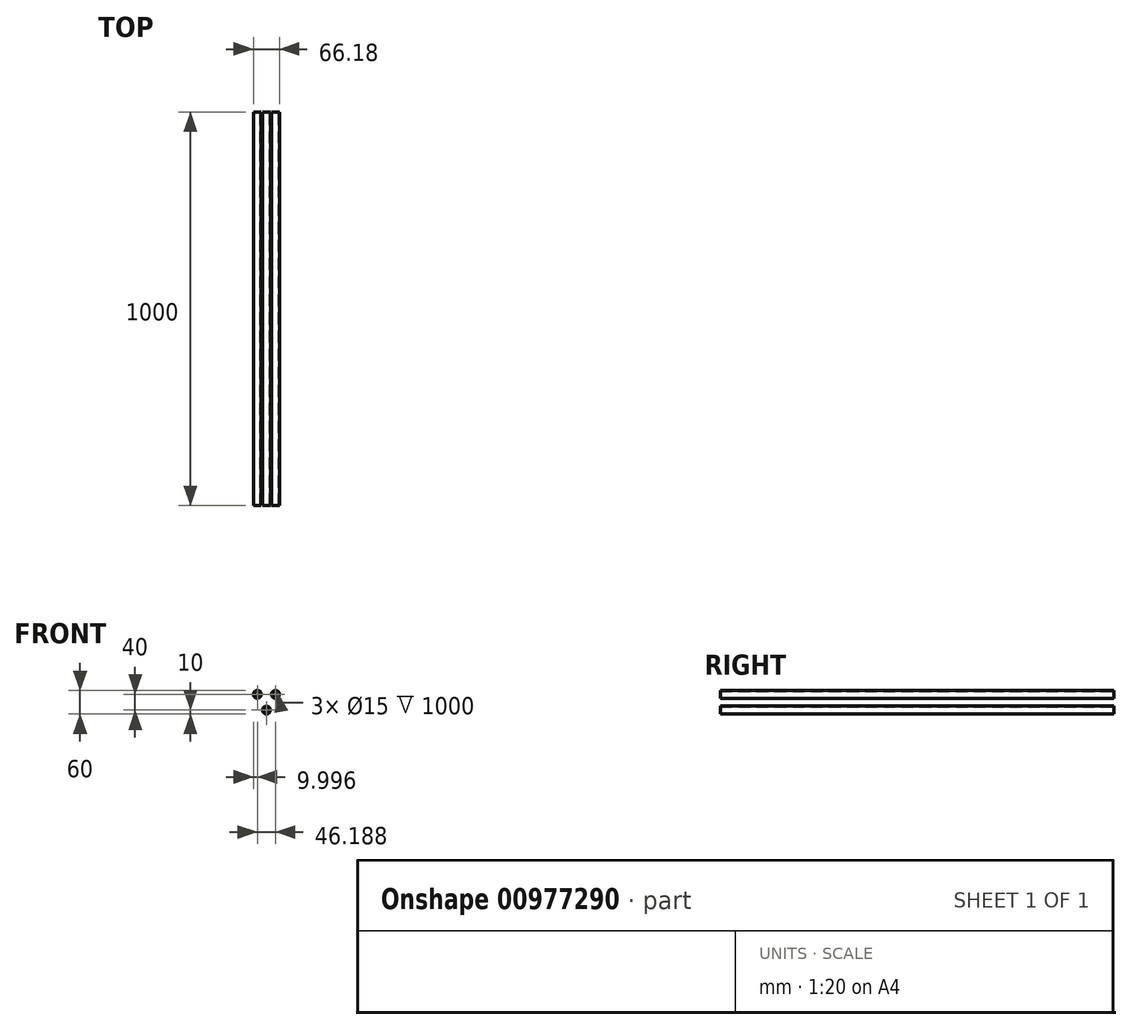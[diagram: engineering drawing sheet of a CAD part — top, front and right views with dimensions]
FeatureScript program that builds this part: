
annotation { "Feature Type Name" : "Feature", "Feature Type Description" : "" }
export const myFeature = defineFeature(function(context is Context, id is Id, definition is map)
    precondition{}
    {
        {
            var Q0;
            Q0=qCreatedBy(makeId("Front.planeOp"),FACE);
            var sketch = newSketch(context, id + "F0", { "sketchPlane" : qUnion([Q0])});
            skCircle(sketch, "E0", {"center": v(0, 0) * mm, "radius": 10 * mm});
            skCircle(sketch, "E1", {"center": v(23.1, 40) * mm, "radius": 10 * mm});
            skCircle(sketch, "E2", {"center": v(-23.1, 40) * mm, "radius": 10 * mm});
            skCircle(sketch, "E3", {"center": v(-23.1, 40) * mm, "radius": 15 * mm});
            skCircle(sketch, "E4", {"center": v(23.1, 40) * mm, "radius": 15 * mm});
            skCircle(sketch, "E5", {"center": v(0, 0) * mm, "radius": 15 * mm});
            skLineSegment(sketch, "E6", {"start": v(0, 0) * mm, "end": v(-23.1, 40) * mm});
            skLineSegment(sketch, "E7", {"start": v(23.1, 40) * mm, "end": v(0, 0) * mm});
            skLineSegment(sketch, "E8", {"start": v(-23.1, 40) * mm, "end": v(23.1, 40) * mm});
            skCircle(sketch, "E9", {"center": v(-23.1, 40) * mm, "radius": 7.5 * mm});
            skCircle(sketch, "E10", {"center": v(23.1, 40) * mm, "radius": 7.5 * mm});
            skCircle(sketch, "E11", {"center": v(0, 0) * mm, "radius": 7.5 * mm});
            skSolve(sketch);
        }
        {
            var Q0;
            {var subQ0=sQuery(id+"F0.wireOp",EDGE,"E6");var subQ1=sQuery(id+"F0.wireOp",EDGE,"E2");var subQ2=makeQuery(id+"F0.imprint","INTERSECT",VERTEX,{"derivedFrom":[subQ1,subQ0]});Q0=makeQuery(id+"F0.imprint","IMPRINT",FACE,{"disambiguationData":[TD([[makeQuery(id+"F0.imprint","IMPRINT",EDGE,{"disambiguationData":[TD([[subQ2,1.0]])],"derivedFrom":subQ1}),1.0]])]});}
            var Q1;
            {var subQ0=sQuery(id+"F0.wireOp",EDGE,"E6");var subQ1=sQuery(id+"F0.wireOp",EDGE,"E2");var subQ2=makeQuery(id+"F0.imprint","INTERSECT",VERTEX,{"derivedFrom":[subQ1,subQ0]});Q1=makeQuery(id+"F0.imprint","IMPRINT",FACE,{"disambiguationData":[TD([[makeQuery(id+"F0.imprint","IMPRINT",EDGE,{"disambiguationData":[TD([[subQ2,-1.0]])],"derivedFrom":subQ1}),1.0]])]});}
            var Q2;
            {var subQ0=sQuery(id+"F0.wireOp",EDGE,"E7");var subQ1=sQuery(id+"F0.wireOp",EDGE,"E1");var subQ2=makeQuery(id+"F0.imprint","INTERSECT",VERTEX,{"derivedFrom":[subQ1,subQ0]});Q2=makeQuery(id+"F0.imprint","IMPRINT",FACE,{"disambiguationData":[TD([[makeQuery(id+"F0.imprint","IMPRINT",EDGE,{"disambiguationData":[TD([[subQ2,-1.0]])],"derivedFrom":subQ1}),1.0]])]});}
            var Q3;
            {var subQ0=sQuery(id+"F0.wireOp",EDGE,"E7");var subQ1=sQuery(id+"F0.wireOp",EDGE,"E1");var subQ2=makeQuery(id+"F0.imprint","INTERSECT",VERTEX,{"derivedFrom":[subQ1,subQ0]});Q3=makeQuery(id+"F0.imprint","IMPRINT",FACE,{"disambiguationData":[TD([[makeQuery(id+"F0.imprint","IMPRINT",EDGE,{"disambiguationData":[TD([[subQ2,1.0]])],"derivedFrom":subQ1}),1.0]])]});}
            var Q4;
            {var subQ0=sQuery(id+"F0.wireOp",EDGE,"E6");var subQ1=sQuery(id+"F0.wireOp",EDGE,"E0");var subQ2=makeQuery(id+"F0.imprint","INTERSECT",VERTEX,{"derivedFrom":[subQ1,subQ0]});Q4=makeQuery(id+"F0.imprint","IMPRINT",FACE,{"disambiguationData":[TD([[makeQuery(id+"F0.imprint","IMPRINT",EDGE,{"disambiguationData":[TD([[subQ2,1.0]])],"derivedFrom":subQ1}),1.0]])]});}
            var Q5;
            {var subQ0=sQuery(id+"F0.wireOp",EDGE,"E6");var subQ1=sQuery(id+"F0.wireOp",EDGE,"E0");var subQ2=makeQuery(id+"F0.imprint","INTERSECT",VERTEX,{"derivedFrom":[subQ1,subQ0]});Q5=makeQuery(id+"F0.imprint","IMPRINT",FACE,{"disambiguationData":[TD([[makeQuery(id+"F0.imprint","IMPRINT",EDGE,{"disambiguationData":[TD([[subQ2,-1.0]])],"derivedFrom":subQ1}),1.0]])]});}
            extrude(context, id + "F1", {"entities" : qUnion([Q0, Q1, Q2, Q3, Q4, Q5]), "depth" : 1000 * mm, "offsetDistance" : 25 * mm});
        }
    });
